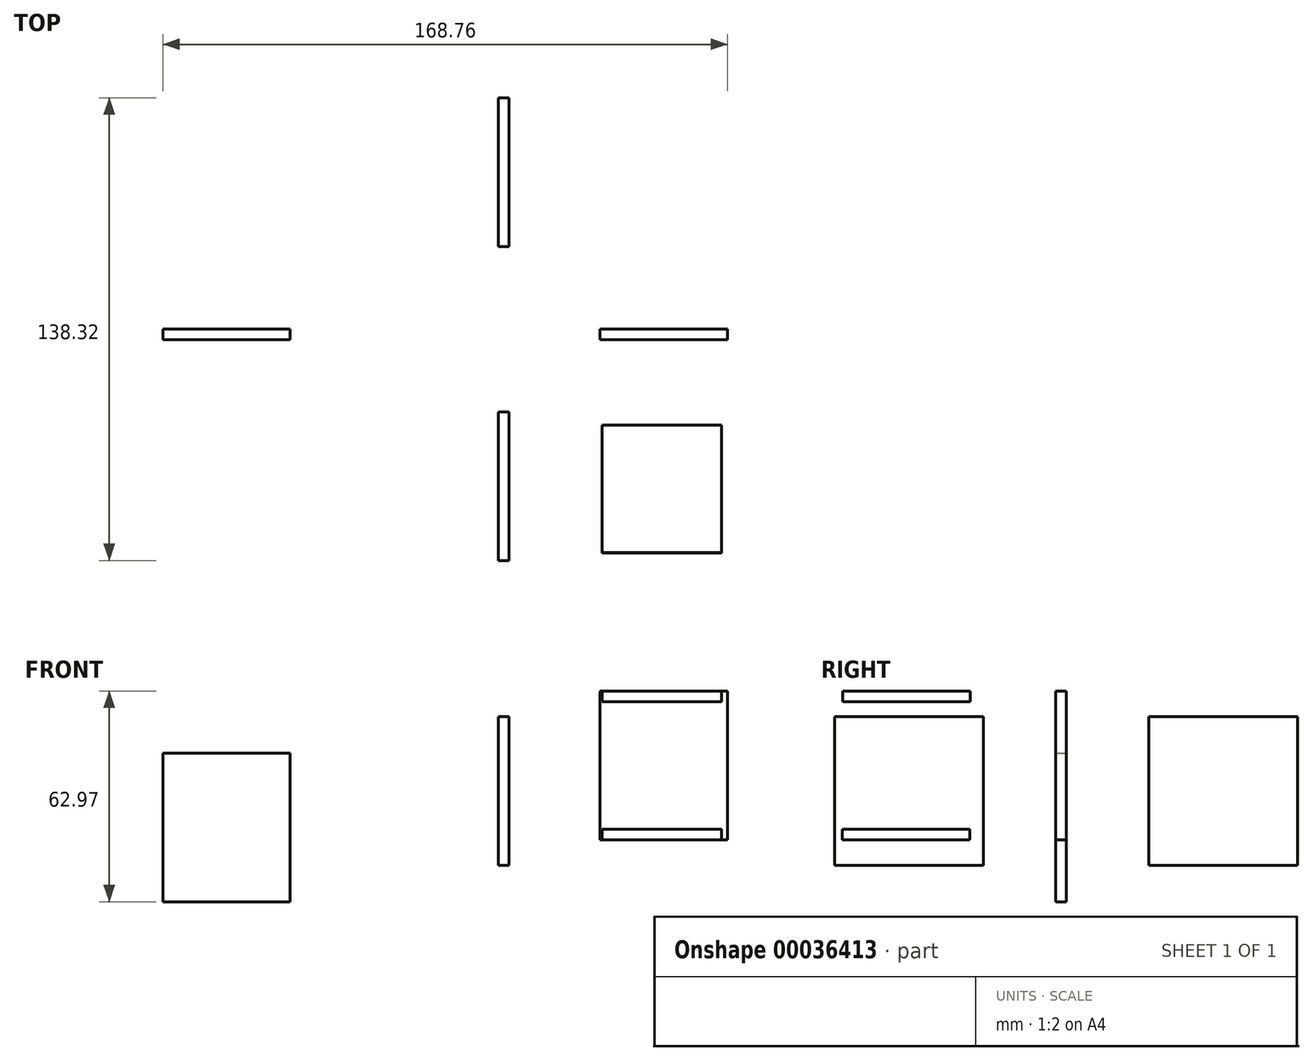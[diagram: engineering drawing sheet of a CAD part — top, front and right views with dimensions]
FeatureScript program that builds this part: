
annotation { "Feature Type Name" : "Feature", "Feature Type Description" : "" }
export const myFeature = defineFeature(function(context is Context, id is Id, definition is map)
    precondition{}
    {
        {
            var Q0;
            Q0=qCreatedBy(makeId("Top.planeOp"),FACE);
            var sketch = newSketch(context, id + "F0", { "sketchPlane" : qUnion([Q0])});
            skLineSegment(sketch, "E0.bottom", {"start": v(66.64, -66.85) * mm, "end": v(31.05, -66.85) * mm});
            skLineSegment(sketch, "E0.top", {"start": v(66.64, -28.75) * mm, "end": v(31.05, -28.75) * mm});
            skLineSegment(sketch, "E0.left", {"start": v(66.64, -66.85) * mm, "end": v(66.64, -28.75) * mm});
            skLineSegment(sketch, "E0.right", {"start": v(31.05, -66.85) * mm, "end": v(31.05, -28.75) * mm});
            skSolve(sketch);
        }
        {
            var Q0;
            Q0=makeQuery(id+"F0.imprint","IMPRINT",FACE,{"disambiguationData":[TD([[makeQuery(id+"F0.imprint","IMPRINT",EDGE,{"derivedFrom":sQuery(id+"F0.wireOp",EDGE,"E0.bottom")}),-1.0]])]});
            cPlane(context, id + "F1", {"entities" : qUnion([Q0]), "cplaneType" : CPlaneType.OFFSET, "offset" : 38.1 * mm, "width" : 152.4 * mm, "height" : 152.4 * mm});
        }
        {
            var Q0;
            Q0=qCreatedBy(id+"F1.planeOp",FACE);
            var sketch = newSketch(context, id + "F2", { "sketchPlane" : qUnion([Q0])});
            skLineSegment(sketch, "E1.bottom", {"start": v(66.63, -28.74) * mm, "end": v(30.98, -28.74) * mm});
            skLineSegment(sketch, "E1.top", {"start": v(66.63, -66.84) * mm, "end": v(30.98, -66.84) * mm});
            skLineSegment(sketch, "E1.left", {"start": v(66.63, -28.74) * mm, "end": v(66.63, -66.84) * mm});
            skLineSegment(sketch, "E1.right", {"start": v(30.98, -28.74) * mm, "end": v(30.98, -66.84) * mm});
            skSolve(sketch);
        }
        {
            var Q0;
            Q0=makeQuery(id+"F2.imprint","IMPRINT",FACE,{"disambiguationData":[TD([[makeQuery(id+"F2.imprint","IMPRINT",EDGE,{"derivedFrom":sQuery(id+"F2.wireOp",EDGE,"E1.bottom")}),1.0]])]});
            extrude(context, id + "F3", {"entities" : qUnion([Q0]), "depth" : 3.17 * mm});
        }
        {
            var Q0;
            Q0=makeQuery(id+"F0.imprint","IMPRINT",FACE,{"disambiguationData":[TD([[makeQuery(id+"F0.imprint","IMPRINT",EDGE,{"derivedFrom":sQuery(id+"F0.wireOp",EDGE,"E0.bottom")}),-1.0]])]});
            extrude(context, id + "F4", {"entities" : qUnion([Q0]), "oppositeDirection" : true, "depth" : 3.17 * mm});
        }
        {
            var Q0;
            Q0=qCreatedBy(makeId("Front.planeOp"),FACE);
            var sketch = newSketch(context, id + "F5", { "sketchPlane" : qUnion([Q0])});
            skLineSegment(sketch, "E2.bottom", {"start": v(68.51, 41.23) * mm, "end": v(30.41, 41.23) * mm});
            skLineSegment(sketch, "E2.top", {"start": v(68.51, -3.22) * mm, "end": v(30.41, -3.22) * mm});
            skLineSegment(sketch, "E2.left", {"start": v(68.51, 41.23) * mm, "end": v(68.51, -3.22) * mm});
            skLineSegment(sketch, "E2.right", {"start": v(30.41, 41.23) * mm, "end": v(30.41, -3.22) * mm});
            skSolve(sketch);
        }
        {
            var Q0;
            Q0=makeQuery(id+"F5.imprint","IMPRINT",FACE,{"disambiguationData":[TD([[makeQuery(id+"F5.imprint","IMPRINT",EDGE,{"derivedFrom":sQuery(id+"F5.wireOp",EDGE,"E2.bottom")}),1.0]])]});
            extrude(context, id + "F6", {"entities" : qUnion([Q0]), "depth" : 3.17 * mm});
        }
        {
            var Q0;
            Q0=qCreatedBy(makeId("Right.planeOp"),FACE);
            var sketch = newSketch(context, id + "F7", { "sketchPlane" : qUnion([Q0])});
            skLineSegment(sketch, "E3.bottom", {"start": v(-24.71, 33.56) * mm, "end": v(-69.16, 33.56) * mm});
            skLineSegment(sketch, "E3.top", {"start": v(-24.71, -10.89) * mm, "end": v(-69.16, -10.89) * mm});
            skLineSegment(sketch, "E3.left", {"start": v(-24.71, 33.56) * mm, "end": v(-24.71, -10.89) * mm});
            skLineSegment(sketch, "E3.right", {"start": v(-69.16, 33.56) * mm, "end": v(-69.16, -10.89) * mm});
            skSolve(sketch);
        }
        {
            var Q0;
            Q0=makeQuery(id+"F7.imprint","IMPRINT",FACE,{"disambiguationData":[TD([[makeQuery(id+"F7.imprint","IMPRINT",EDGE,{"derivedFrom":sQuery(id+"F7.wireOp",EDGE,"E3.bottom")}),1.0]])]});
            extrude(context, id + "F8", {"entities" : qUnion([Q0]), "depth" : 3.17 * mm});
        }
        {
            var Q0;
            Q0=qCreatedBy(makeId("Front.planeOp"),FACE);
            var sketch = newSketch(context, id + "F9", { "sketchPlane" : qUnion([Q0])});
            skLineSegment(sketch, "E4.bottom", {"start": v(-62.15, 22.75) * mm, "end": v(-100.25, 22.75) * mm});
            skLineSegment(sketch, "E4.top", {"start": v(-62.15, -21.7) * mm, "end": v(-100.25, -21.7) * mm});
            skLineSegment(sketch, "E4.left", {"start": v(-62.15, 22.75) * mm, "end": v(-62.15, -21.7) * mm});
            skLineSegment(sketch, "E4.right", {"start": v(-100.25, 22.75) * mm, "end": v(-100.25, -21.7) * mm});
            skSolve(sketch);
        }
        {
            var Q0;
            Q0=makeQuery(id+"F9.imprint","IMPRINT",FACE,{"disambiguationData":[TD([[makeQuery(id+"F9.imprint","IMPRINT",EDGE,{"derivedFrom":sQuery(id+"F9.wireOp",EDGE,"E4.bottom")}),1.0]])]});
            extrude(context, id + "F10", {"entities" : qUnion([Q0]), "depth" : 3.17 * mm});
        }
        {
            var Q0;
            Q0=makeQuery(id+"F8.opExtrude","SWEPT_BODY",BODY,{"disambiguationData":[OSD([sQuery(id+"F7.wireOp",EDGE,"E3.bottom"),sQuery(id+"F7.wireOp",EDGE,"E3.top"),sQuery(id+"F7.wireOp",EDGE,"E3.left"),sQuery(id+"F7.wireOp",EDGE,"E3.right")])]});
            var Q1;
            Q1=qCreatedBy(makeId("Front.planeOp"),FACE);
            mirror(context, id + "F11", {"entities" : qUnion([Q0]), "mirrorPlane" : qUnion([Q1])});
        }
    });
